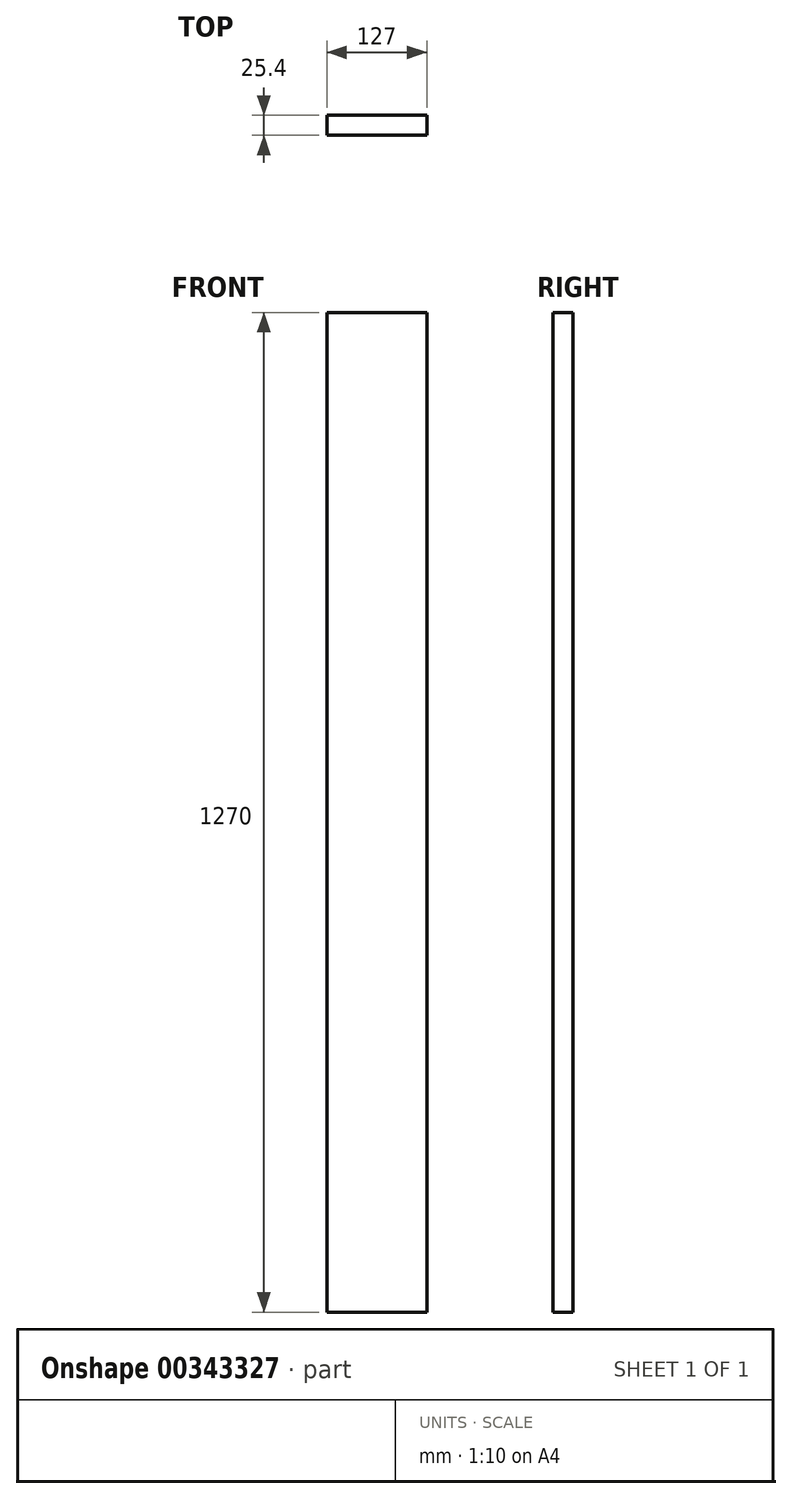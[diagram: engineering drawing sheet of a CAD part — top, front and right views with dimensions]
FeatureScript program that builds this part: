
annotation { "Feature Type Name" : "Feature", "Feature Type Description" : "" }
export const myFeature = defineFeature(function(context is Context, id is Id, definition is map)
    precondition{}
    {
        {
            var Q0;
            Q0=qCreatedBy(makeId("Top.planeOp"),FACE);
            var sketch = newSketch(context, id + "F0", { "sketchPlane" : qUnion([Q0])});
            skLineSegment(sketch, "E0.bottom", {"start": v(-67.2, 12.7) * mm, "end": v(59.8, 12.7) * mm});
            skLineSegment(sketch, "E0.top", {"start": v(-67.2, -12.7) * mm, "end": v(59.8, -12.7) * mm});
            skLineSegment(sketch, "E0.left", {"start": v(-67.2, 12.7) * mm, "end": v(-67.2, -12.7) * mm});
            skLineSegment(sketch, "E0.right", {"start": v(59.8, 12.7) * mm, "end": v(59.8, -12.7) * mm});
            skPoint(sketch, "E0.middle", {"position": v(-3.7, 0) * mm});
            skSolve(sketch);
        }
        {
            var Q0;
            Q0=makeQuery(id+"F0.imprint","IMPRINT",FACE,{"disambiguationData":[TD([[makeQuery(id+"F0.imprint","IMPRINT",EDGE,{"derivedFrom":sQuery(id+"F0.wireOp",EDGE,"E0.bottom")}),-1.0]])]});
            extrude(context, id + "F1", {"entities" : qUnion([Q0]), "depth" : 1270 * mm});
        }
    });
